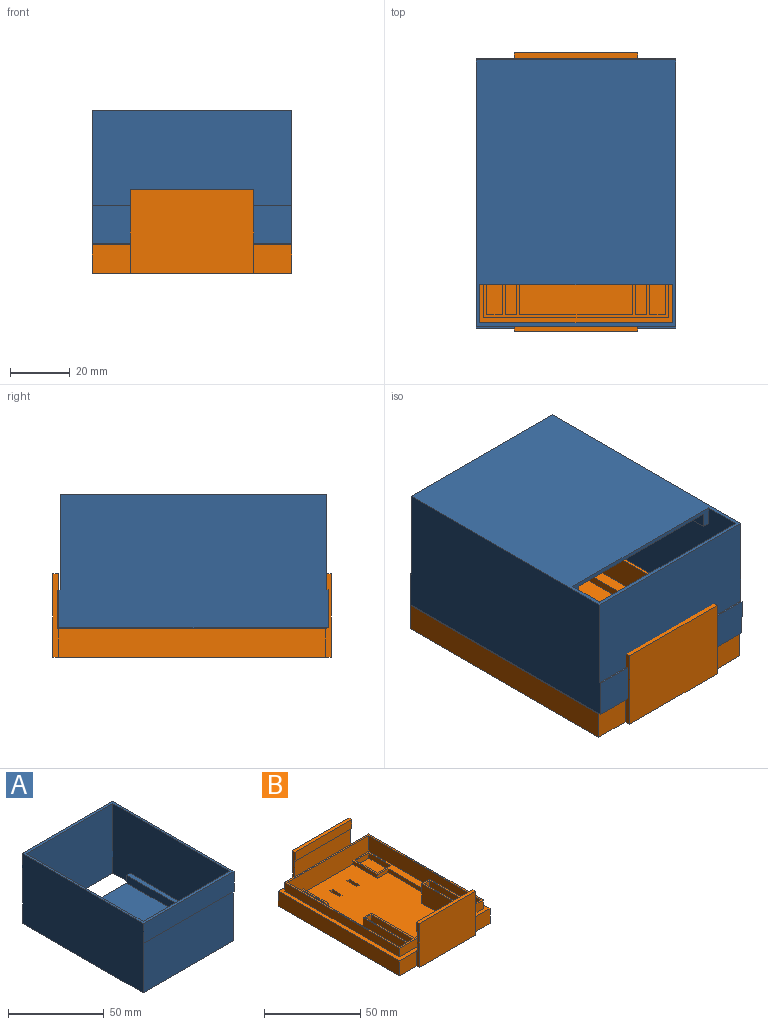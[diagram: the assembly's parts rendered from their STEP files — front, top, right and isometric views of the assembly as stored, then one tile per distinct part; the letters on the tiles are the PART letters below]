
ASSEMBLY  parts=2 mates=1
PART A: 22 faces, bbox 66.7x89.9x44.5 mm
  f0: plane 66.68x31.75mm, normal (0,1,0), area 2116.9mm2, adj f4,f6,f7,f18
  f1: plane 73.66x64.14mm, normal (0,0,1), area 4466.1mm2, adj f2,f9,f10,f11,f12,f13,f15,f16
  f2: plane 86.36x44.45mm, normal (-1,0,0), area 3487.1mm2, adj f1,f3,f7,f8,f10,f11,f13,f14
  f3: plane 89.9x66.68mm, normal (0,0,1), area 455.4mm2, adj f2,f4,f6,f8,f9,f10,f19,f21
  f4: plane 89.9x44.45mm, normal (-1,0,0), area 3964.3mm2, adj f0,f3,f5,f7,f18,f19,f20,f21
  f5: plane 66.68x31.75mm, normal (0,-1,0), area 2117.2mm2, adj f4,f6,f7,f20
  f6: plane 89.9x44.45mm, normal (1,0,0), area 3964.3mm2, adj f0,f3,f5,f7,f18,f19,f20,f21
  f7: plane 88.9x66.68mm, normal (0,0,-1), area 5112.9mm2, adj f0,f2,f4,f5,f6,f8,f9,f11
  f8: plane 64.14x44.45mm, normal (0,-1,0), area 2850.8mm2, adj f2,f3,f7,f9
  f9: plane 86.36x44.45mm, normal (1,0,0), area 3487.1mm2, adj f1,f3,f7,f8,f10,f11,f15,f17
  f10: plane 64.14x43.18mm, normal (0,1,0), area 2769.3mm2, adj f1,f2,f3,f9
  f11: plane 64.14x6.35mm, normal (0,1,0), area 107.3mm2, adj f1,f2,f7,f9,f12,f14,f16,f17
  f12: plane 50.8x5.08mm, normal (-1,0,0), area 258.1mm2, adj f1,f11,f13,f14
  f13: plane 5.08x2.54mm, normal (0,-1,0), area 12.9mm2, adj f1,f2,f12,f14
  f14: plane 50.8x2.54mm, normal (0,0,1), area 129mm2, adj f2,f11,f12,f13
  f15: plane 5.08x2.54mm, normal (0,-1,0), area 12.9mm2, adj f1,f9,f16,f17
  f16: plane 50.8x5.08mm, normal (1,0,0), area 258.1mm2, adj f1,f11,f15,f17
  f17: plane 50.8x2.54mm, normal (0,0,1), area 129mm2, adj f9,f11,f15,f16
  f18: plane 66.68x0.5mm, normal (0,0,-1), area 33.3mm2, adj f0,f4,f6,f19
  f19: plane 66.68x12.7mm, normal (0,1,0), area 846.8mm2, adj f3,f4,f6,f18
  f20: plane 66.68x0.5mm, normal (0,0,-1), area 33.3mm2, adj f4,f5,f6,f21
  f21: plane 66.68x12.7mm, normal (0,-1,0), area 846.5mm2, adj f3,f4,f6,f20
PART B: 139 faces, bbox 66.7x92.9x27.9 mm
  f0: plane 41.28x5.72mm, normal (0,1,0), area 235.9mm2, adj f1,f107,f108,f110
  f1: plane 27.94x2mm, normal (-1,0,0), area 49.4mm2, adj f0,f8,f10,f11,f108,f109,f110,f111
  f2: plane 12.7x9.53mm, normal (0,-1,0), area 121mm2, adj f8,f10,f12,f107
  f3: plane 41.28x5.72mm, normal (0,-1,0), area 235.9mm2, adj f4,f102,f103,f105
  f4: plane 27.94x2mm, normal (1,0,0), area 49.4mm2, adj f3,f5,f8,f10,f103,f104,f105,f106
  f5: plane 12.7x9.53mm, normal (0,1,0), area 121mm2, adj f4,f8,f10,f12
  f6: plane 61.6x0.01mm, normal (0,0,1), area 0.7mm2, adj f15,f16,f17,f80
  f7: plane 81.82x59.6mm, normal (0,0,1), area 3789.1mm2, adj f18,f19,f20,f22,f23,f24,f25,f26
  f8: plane 89.92x66.68mm, normal (0,0,1), area 805.8mm2, adj f1,f2,f4,f5,f11,f12,f13,f14
  f9: plane 51.06x11.7mm, normal (0,0,1), area 187.7mm2, adj f22,f23,f24,f39,f40,f41,f42,f91
  f10: plane 92.9x66.68mm, normal (0,0,-1), area 6064.9mm2, adj f1,f2,f4,f5,f11,f12,f13,f14
  f11: plane 12.7x9.53mm, normal (0,-1,0), area 121mm2, adj f1,f8,f10,f14
  f12: plane 88.9x9.53mm, normal (1,0,0), area 846.8mm2, adj f2,f5,f8,f10
  f13: plane 12.7x9.53mm, normal (0,1,0), area 121mm2, adj f8,f10,f14,f102
  f14: plane 88.9x9.53mm, normal (-1,0,0), area 846.8mm2, adj f8,f10,f11,f13
  f15: plane 61.6x6.99mm, normal (0,1,0), area 430.2mm2, adj f6,f8,f16,f17
  f16: plane 6.99x0.01mm, normal (-1,0,0), area 0.1mm2, adj f6,f8,f15,f80
  f17: plane 6.99x0.01mm, normal (1,0,0), area 0.1mm2, adj f6,f8,f15,f80
  f18: plane 11.7x2.46mm, normal (0,1,0), area 28.8mm2, adj f7,f19,f21,f72
  f19: plane 18.04x2.46mm, normal (-1,0,0), area 44.4mm2, adj f7,f18,f20,f21
  f20: plane 7.7x2.46mm, normal (0,-1,0), area 18.9mm2, adj f7,f19,f21,f99
  f21: plane 51.06x11.7mm, normal (0,0,1), area 187.7mm2, adj f18,f19,f20,f35,f36,f37,f38,f72
  f22: plane 18.04x2.46mm, normal (1,0,0), area 44.4mm2, adj f7,f9,f23,f24
  f23: plane 11.7x2.46mm, normal (0,1,0), area 28.8mm2, adj f7,f9,f22,f91
  f24: plane 7.7x2.46mm, normal (0,-1,0), area 18.9mm2, adj f7,f9,f22,f97
  f25: plane 2.54x1.91mm, normal (0,1,0), area 4.8mm2, adj f7,f10,f26,f28
  f26: plane 7.24x2.54mm, normal (-1,0,0), area 18.4mm2, adj f7,f10,f25,f27
  f27: plane 2.54x1.91mm, normal (0,-1,0), area 4.8mm2, adj f7,f10,f26,f28
  f28: plane 7.24x2.54mm, normal (1,0,0), area 18.4mm2, adj f7,f10,f25,f27
  f29: plane 7.25x2.54mm, normal (1,0,0), area 18.4mm2, adj f7,f10,f30,f32
  f30: plane 2.54x1.9mm, normal (0,1,0), area 4.8mm2, adj f7,f10,f29,f31
  f31: plane 7.25x2.54mm, normal (-1,0,0), area 18.4mm2, adj f7,f10,f30,f32
  f32: plane 2.54x1.9mm, normal (0,-1,0), area 4.8mm2, adj f7,f10,f29,f31
  f33: plane 81.82x59.6mm, normal (0,0,-1), area 3855.5mm2, adj f35,f36,f37,f38,f39,f40,f41,f42
  f34: plane 81.82x59.6mm, normal (0,0,1), area 4166.7mm2, adj f43,f44,f45,f46,f47,f48,f49,f50
  f35: plane 9.7x3.46mm, normal (0,-1,0), area 33.6mm2, adj f21,f33,f36,f38
  f36: plane 16.04x3.46mm, normal (1,0,0), area 55.5mm2, adj f21,f33,f35,f37
  f37: plane 9.7x3.46mm, normal (0,1,0), area 33.6mm2, adj f21,f33,f36,f38
  f38: plane 16.04x3.46mm, normal (-1,0,0), area 55.5mm2, adj f21,f33,f35,f37
  f39: plane 16.04x3.46mm, normal (-1,0,0), area 55.5mm2, adj f9,f33,f40,f42
  f40: plane 9.7x3.46mm, normal (0,-1,0), area 33.6mm2, adj f9,f33,f39,f41
  f41: plane 16.04x3.46mm, normal (1,0,0), area 55.5mm2, adj f9,f33,f40,f42
  f42: plane 9.7x3.46mm, normal (0,1,0), area 33.6mm2, adj f9,f33,f39,f41
  f43: plane 3.91x0.54mm, normal (0,-1,0), area 2.1mm2, adj f33,f34,f44,f46
  f44: plane 9.24x0.54mm, normal (1,0,0), area 5mm2, adj f33,f34,f43,f45
  f45: plane 3.91x0.54mm, normal (0,1,0), area 2.1mm2, adj f33,f34,f44,f46
  f46: plane 9.24x0.54mm, normal (-1,0,0), area 5mm2, adj f33,f34,f43,f45
  f47: plane 9.25x0.54mm, normal (-1,0,0), area 5mm2, adj f33,f34,f48,f50
  f48: plane 3.9x0.54mm, normal (0,-1,0), area 2.1mm2, adj f33,f34,f47,f49
  f49: plane 9.25x0.54mm, normal (1,0,0), area 5mm2, adj f33,f34,f48,f50
  f50: plane 3.9x0.54mm, normal (0,1,0), area 2.1mm2, adj f33,f34,f47,f49
  f51: plane 5.24x0.54mm, normal (0,1,0), area 2.8mm2, adj f33,f34,f54,f70
  f52: plane 5.87x0.54mm, normal (0,1,0), area 3.2mm2, adj f33,f34,f53,f54
  f53: plane 31.74x0.54mm, normal (-1,0,0), area 17.1mm2, adj f33,f34,f52,f65
  f54: plane 31.74x0.54mm, normal (1,0,0), area 17.1mm2, adj f33,f34,f51,f52
  f55: plane 5.87x0.54mm, normal (0,1,0), area 3.2mm2, adj f33,f34,f56,f57
  f56: plane 31.74x0.54mm, normal (-1,0,0), area 17.1mm2, adj f33,f34,f55,f64
  f57: plane 31.74x0.54mm, normal (1,0,0), area 17.1mm2, adj f33,f34,f55,f65
  f58: plane 59.6x0.54mm, normal (0,-1,0), area 32.2mm2, adj f33,f34,f62,f69
  f59: plane 4x0.54mm, normal (0,1,0), area 2.2mm2, adj f33,f34,f60,f62
  f60: plane 33.02x0.54mm, normal (1,0,0), area 17.8mm2, adj f33,f34,f59,f61
  f61: plane 4x0.54mm, normal (0,-1,0), area 2.2mm2, adj f33,f34,f60,f63
  f62: plane 18.05x0.54mm, normal (1,0,0), area 9.7mm2, adj f33,f34,f58,f59
  f63: plane 30.75x0.54mm, normal (1,0,0), area 16.6mm2, adj f33,f34,f61,f64
  f64: plane 5.24x0.54mm, normal (0,1,0), area 2.8mm2, adj f33,f34,f56,f63
  f65: plane 37.37x0.54mm, normal (0,1,0), area 20.2mm2, adj f33,f34,f53,f57
  f66: plane 33.02x0.54mm, normal (-1,0,0), area 17.8mm2, adj f33,f34,f67,f68
  f67: plane 4x0.54mm, normal (0,1,0), area 2.2mm2, adj f33,f34,f66,f69
  f68: plane 4x0.54mm, normal (0,-1,0), area 2.2mm2, adj f33,f34,f66,f70
  f69: plane 18.05x0.54mm, normal (-1,0,0), area 9.7mm2, adj f33,f34,f58,f67
  f70: plane 30.75x0.54mm, normal (-1,0,0), area 16.6mm2, adj f33,f34,f51,f68
  f71: plane 83.82x5.48mm, normal (1,0,0), area 458.9mm2, adj f8,f80,f82,f84
  f72: plane 81.82x12.46mm, normal (-1,0,0), area 893.9mm2, adj f7,f18,f21,f84,f92,f94,f98
  f73: plane 30.75x12.46mm, normal (-1,0,0), area 383.1mm2, adj f74,f83,f84,f100
  f74: plane 12.46x3.87mm, normal (0,1,0), area 48.3mm2, adj f73,f75,f84,f100
  f75: plane 30.75x12.46mm, normal (1,0,0), area 383.1mm2, adj f74,f83,f84,f100
  f76: plane 30.75x12.46mm, normal (-1,0,0), area 383.1mm2, adj f77,f81,f84,f101
  f77: plane 12.46x3.87mm, normal (0,1,0), area 48.3mm2, adj f76,f78,f84,f101
  f78: plane 30.75x12.46mm, normal (1,0,0), area 383.1mm2, adj f77,f81,f84,f101
  f79: plane 83.82x5.48mm, normal (-1,0,0), area 458.9mm2, adj f8,f80,f82,f84
  f80: plane 61.6x12.46mm, normal (0,-1,0), area 767.5mm2, adj f6,f16,f17,f71,f79,f84
  f81: plane 12.46x3.87mm, normal (0,-1,0), area 48.3mm2, adj f76,f78,f84,f101
  f82: plane 61.6x5.48mm, normal (0,1,0), area 337.2mm2, adj f8,f71,f79,f84
  f83: plane 12.46x3.87mm, normal (0,-1,0), area 48.3mm2, adj f73,f75,f84,f100
  f84: plane 83.82x61.6mm, normal (0,0,1), area 421.4mm2, adj f71,f72,f73,f74,f75,f76,f77,f78
  f85: plane 37.37x12.46mm, normal (0,1,0), area 465.6mm2, adj f7,f84,f87,f90
  f86: plane 12.46x5.24mm, normal (0,1,0), area 65.3mm2, adj f7,f84,f88,f91
  f87: plane 31.74x12.46mm, normal (1,0,0), area 395.5mm2, adj f7,f84,f85,f95
  f88: plane 31.74x12.46mm, normal (-1,0,0), area 395.5mm2, adj f7,f84,f86,f95
  f89: plane 31.74x12.46mm, normal (1,0,0), area 395.5mm2, adj f7,f84,f92,f93
  f90: plane 31.74x12.46mm, normal (-1,0,0), area 395.5mm2, adj f7,f84,f85,f93
  f91: plane 81.82x12.46mm, normal (1,0,0), area 893.9mm2, adj f7,f9,f23,f84,f86,f94,f96
  f92: plane 12.46x5.24mm, normal (0,1,0), area 65.3mm2, adj f7,f72,f84,f89
  f93: plane 12.46x5.87mm, normal (0,1,0), area 73.2mm2, adj f7,f84,f89,f90
  f94: plane 59.6x12.46mm, normal (0,-1,0), area 742.6mm2, adj f7,f72,f84,f91
  f95: plane 12.46x5.87mm, normal (0,1,0), area 73.2mm2, adj f7,f84,f87,f88
  f96: plane 4x2.46mm, normal (0,-1,0), area 9.8mm2, adj f7,f9,f91,f97
  f97: plane 33.02x2.46mm, normal (1,0,0), area 81.2mm2, adj f7,f9,f24,f96
  f98: plane 4x2.46mm, normal (0,-1,0), area 9.8mm2, adj f7,f21,f72,f99
  f99: plane 33.02x2.46mm, normal (-1,0,0), area 81.2mm2, adj f7,f20,f21,f98
  f100: plane 30.75x3.87mm, normal (0,0,1), area 119.1mm2, adj f73,f74,f75,f83
  f101: plane 30.75x3.87mm, normal (0,0,1), area 119.1mm2, adj f76,f77,f78,f81
  f102: plane 27.94x2mm, normal (-1,0,0), area 49.4mm2, adj f3,f8,f10,f13,f103,f104,f105,f106
  f103: plane 41.28x2mm, normal (0,0,1), area 82.6mm2, adj f3,f4,f102,f104
  f104: plane 41.28x27.94mm, normal (0,1,0), area 1153.2mm2, adj f4,f10,f102,f103
  f105: plane 41.28x0.51mm, normal (0,0,-1), area 21mm2, adj f3,f4,f102,f106
  f106: plane 41.28x12.7mm, normal (0,-1,0), area 524.2mm2, adj f4,f8,f102,f105
  f107: plane 27.94x2mm, normal (1,0,0), area 49.4mm2, adj f0,f2,f8,f10,f108,f109,f110,f111
  f108: plane 41.28x2mm, normal (0,0,1), area 82.6mm2, adj f0,f1,f107,f109
  f109: plane 41.28x27.94mm, normal (0,-1,0), area 1153.2mm2, adj f1,f10,f107,f108
  f110: plane 41.28x0.51mm, normal (0,0,-1), area 21mm2, adj f0,f1,f107,f111
  f111: plane 41.28x12.7mm, normal (0,1,0), area 524.2mm2, adj f1,f8,f107,f110
  f112: plane 30.75x3.87mm, normal (0,0,1), area 119.1mm2, adj f113,f114,f115,f116
  f113: plane 3.87x0.54mm, normal (0,-1,0), area 2.1mm2, adj f112,f114,f116,f117
  f114: plane 30.75x0.54mm, normal (1,0,0), area 16.6mm2, adj f112,f113,f115,f117
  f115: plane 3.87x0.54mm, normal (0,1,0), area 2.1mm2, adj f112,f114,f116,f117
  f116: plane 30.75x0.54mm, normal (-1,0,0), area 16.6mm2, adj f112,f113,f115,f117
  f117: plane 30.75x3.87mm, normal (0,0,-1), area 119.1mm2, adj f113,f114,f115,f116
  f118: plane 61.6x0.54mm, normal (0,1,0), area 33.3mm2, adj f119,f121,f126,f132
  f119: plane 83.82x0.54mm, normal (1,0,0), area 45.3mm2, adj f118,f120,f126,f132
  f120: plane 61.6x0.54mm, normal (0,-1,0), area 33.3mm2, adj f119,f121,f126,f132
  f121: plane 83.82x0.54mm, normal (-1,0,0), area 45.3mm2, adj f118,f120,f126,f132
  f122: plane 85.82x6.99mm, normal (1,0,0), area 599.5mm2, adj f123,f125,f126,f127
  f123: plane 63.6x6.99mm, normal (0,1,0), area 444.2mm2, adj f122,f124,f126,f127
  f124: plane 85.82x6.99mm, normal (-1,0,0), area 599.5mm2, adj f123,f125,f126,f127
  f125: plane 63.6x6.99mm, normal (0,-1,0), area 444.2mm2, adj f122,f124,f126,f127
  f126: plane 85.82x63.6mm, normal (0,0,-1), area 294.8mm2, adj f118,f119,f120,f121,f122,f123,f124,f125
  f127: plane 86.9x64.68mm, normal (0,0,-1), area 162.5mm2, adj f122,f123,f124,f125,f128,f129,f130,f131
  f128: plane 86.9x7.53mm, normal (1,0,0), area 653.9mm2, adj f127,f129,f131,f132
  f129: plane 64.68x7.53mm, normal (0,-1,0), area 486.7mm2, adj f127,f128,f130,f132
  f130: plane 86.9x7.53mm, normal (-1,0,0), area 653.9mm2, adj f127,f129,f131,f132
  f131: plane 64.68x7.53mm, normal (0,1,0), area 486.7mm2, adj f127,f128,f130,f132
  f132: plane 86.9x64.68mm, normal (0,0,1), area 457.4mm2, adj f118,f119,f120,f121,f128,f129,f130,f131
  f133: plane 30.75x3.87mm, normal (0,0,1), area 119.1mm2, adj f134,f135,f136,f137
  f134: plane 3.87x0.54mm, normal (0,-1,0), area 2.1mm2, adj f133,f135,f137,f138
  f135: plane 30.75x0.54mm, normal (1,0,0), area 16.6mm2, adj f133,f134,f136,f138
  f136: plane 3.87x0.54mm, normal (0,1,0), area 2.1mm2, adj f133,f135,f137,f138
  f137: plane 30.75x0.54mm, normal (-1,0,0), area 16.6mm2, adj f133,f134,f136,f138
  f138: plane 30.75x3.87mm, normal (0,0,-1), area 119.1mm2, adj f134,f135,f136,f137
PLACE A rot(axis=(-1,0,0),180deg) t=(-12.13,21.03,9.05)mm
PLACE B rot(axis=(0.01,0.99,0.1),0deg) t=(-13.26,0.51,-45.23)mm
MATE slider B.f8 <-> A.f3  axis (0,0,1) through (20.08,55.12,-35.7)mm
